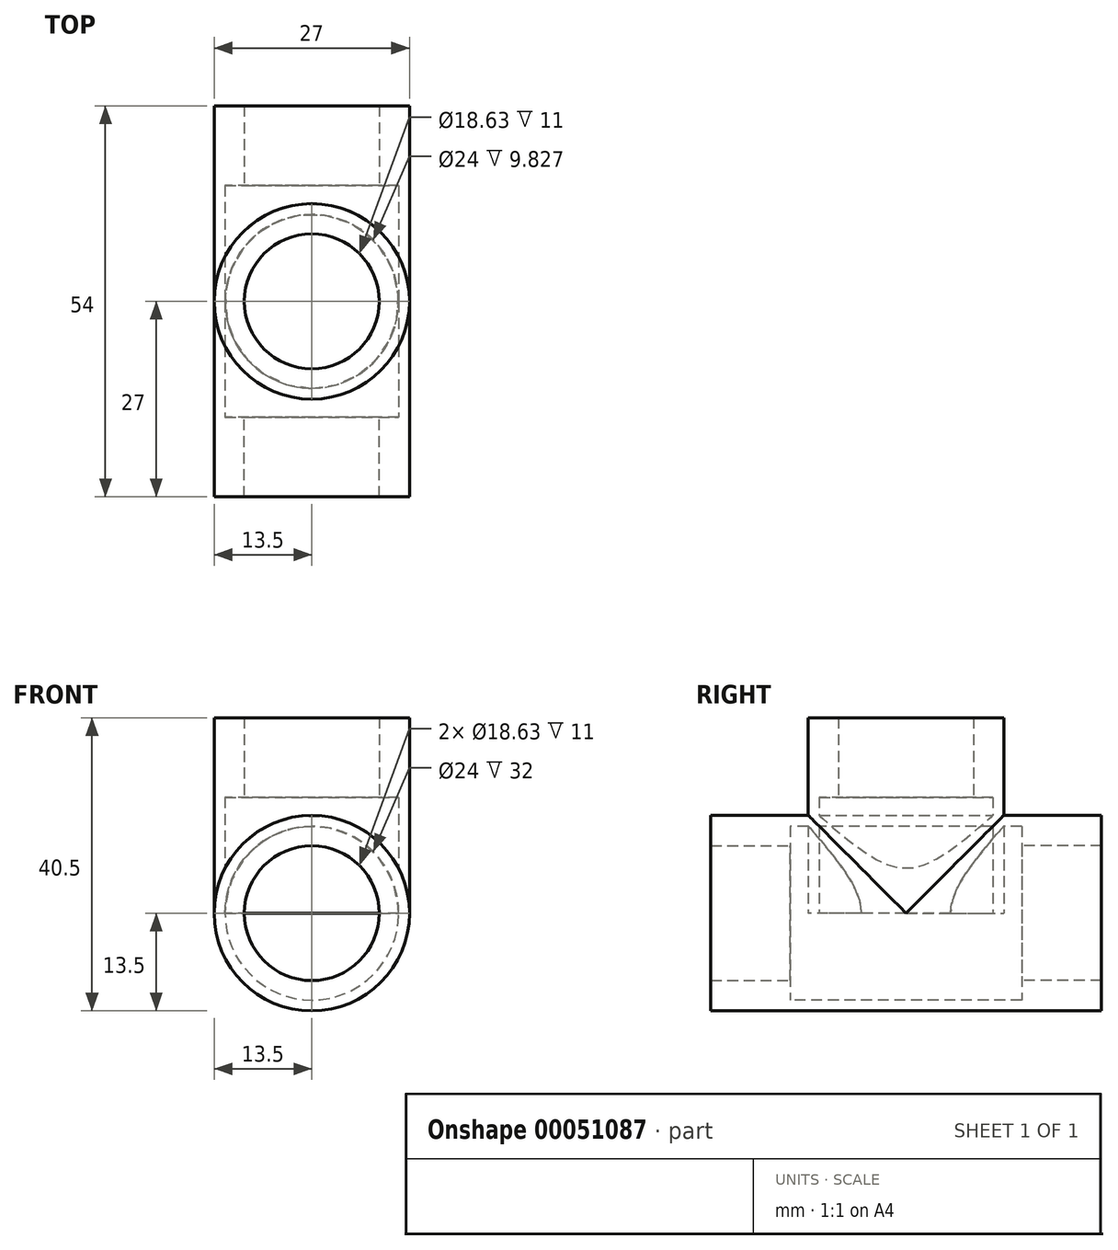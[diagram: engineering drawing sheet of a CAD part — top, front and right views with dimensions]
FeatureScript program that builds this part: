
annotation { "Feature Type Name" : "Feature", "Feature Type Description" : "" }
export const myFeature = defineFeature(function(context is Context, id is Id, definition is map)
    precondition{}
    {
        {
            var Q0;
            Q0=qCreatedBy(makeId("Front.planeOp"),FACE);
            var sketch = newSketch(context, id + "F0", { "sketchPlane" : qUnion([Q0])});
            skCircle(sketch, "E0", {"center": v(0, 0) * mm, "radius": 9.32 * mm});
            skCircle(sketch, "E1", {"center": v(0, 0) * mm, "radius": 13.5 * mm});
            skSolve(sketch);
        }
        {
            var Q0;
            Q0=qSketchRegion(id+"F0",true);
            extrude(context, id + "F1", {"entities" : qUnion([Q0]), "depth" : 11 * mm});
        }
        {
            var Q0;
            Q0=makeQuery(id+"F1.opExtrude","CAP_FACE",FACE,{"disambiguationData":[OSD([sQuery(id+"F0.wireOp",EDGE,"E0"),sQuery(id+"F0.wireOp",EDGE,"E1")])],"isStart":true});
            var sketch = newSketch(context, id + "F2", { "sketchPlane" : qUnion([Q0])});
            skCircle(sketch, "E2", {"center": v(0, 0) * mm, "radius": 13.5 * mm});
            skCircle(sketch, "E3", {"center": v(0, 0) * mm, "radius": 12 * mm});
            skSolve(sketch);
        }
        {
            var Q0;
            Q0=qSketchRegion(id+"F2",true);
            extrude(context, id + "F3", {"entities" : qUnion([Q0]), "operationType" : NewBodyOperationType.ADD, "depth" : (27 * 2 - 22) * mm});
        }
        {
            var Q0;
            Q0=makeQuery(id+"F3.opExtrude","CAP_FACE",FACE,{"disambiguationData":[OSD([sQuery(id+"F2.wireOp",EDGE,"E2"),sQuery(id+"F2.wireOp",EDGE,"E3")])],"isStart":false});
            var sketch = newSketch(context, id + "F4", { "sketchPlane" : qUnion([Q0])});
            skCircle(sketch, "E4", {"center": v(0, 0) * mm, "radius": 13.5 * mm});
            skCircle(sketch, "E5", {"center": v(0, 0) * mm, "radius": 9.32 * mm});
            skSolve(sketch);
        }
        {
            var Q0;
            Q0=qSketchRegion(id+"F4",true);
            extrude(context, id + "F5", {"entities" : qUnion([Q0]), "operationType" : NewBodyOperationType.ADD, "depth" : 11 * mm});
        }
        {
            var Q0;
            Q0=qCreatedBy(makeId("Top.planeOp"),FACE);
            var sketch = newSketch(context, id + "F6", { "sketchPlane" : qUnion([Q0])});
            skCircle(sketch, "E6", {"center": v(0, 16) * mm, "radius": 13.5 * mm});
            skCircle(sketch, "E7", {"center": v(0, 16) * mm, "radius": 12 * mm});
            skSolve(sketch);
        }
        {
            var Q0;
            Q0=qSketchRegion(id+"F6",true);
            extrude(context, id + "F7", {"entities" : qUnion([Q0]), "operationType" : NewBodyOperationType.ADD, "depth" : 16 * mm});
        }
        {
            var Q0;
            Q0=makeQuery(id+"F7.opExtrude","CAP_FACE",FACE,{"disambiguationData":[OSD([sQuery(id+"F6.wireOp",EDGE,"E6"),sQuery(id+"F6.wireOp",EDGE,"E7")])],"isStart":false});
            var sketch = newSketch(context, id + "F8", { "sketchPlane" : qUnion([Q0])});
            skCircle(sketch, "E8", {"center": v(0, 16) * mm, "radius": 9.32 * mm});
            skCircle(sketch, "E9", {"center": v(0, 16) * mm, "radius": 13.5 * mm});
            skSolve(sketch);
        }
        {
            var Q0;
            Q0=qSketchRegion(id+"F8",true);
            extrude(context, id + "F9", {"entities" : qUnion([Q0]), "operationType" : NewBodyOperationType.ADD, "depth" : 11 * mm});
        }
    });
